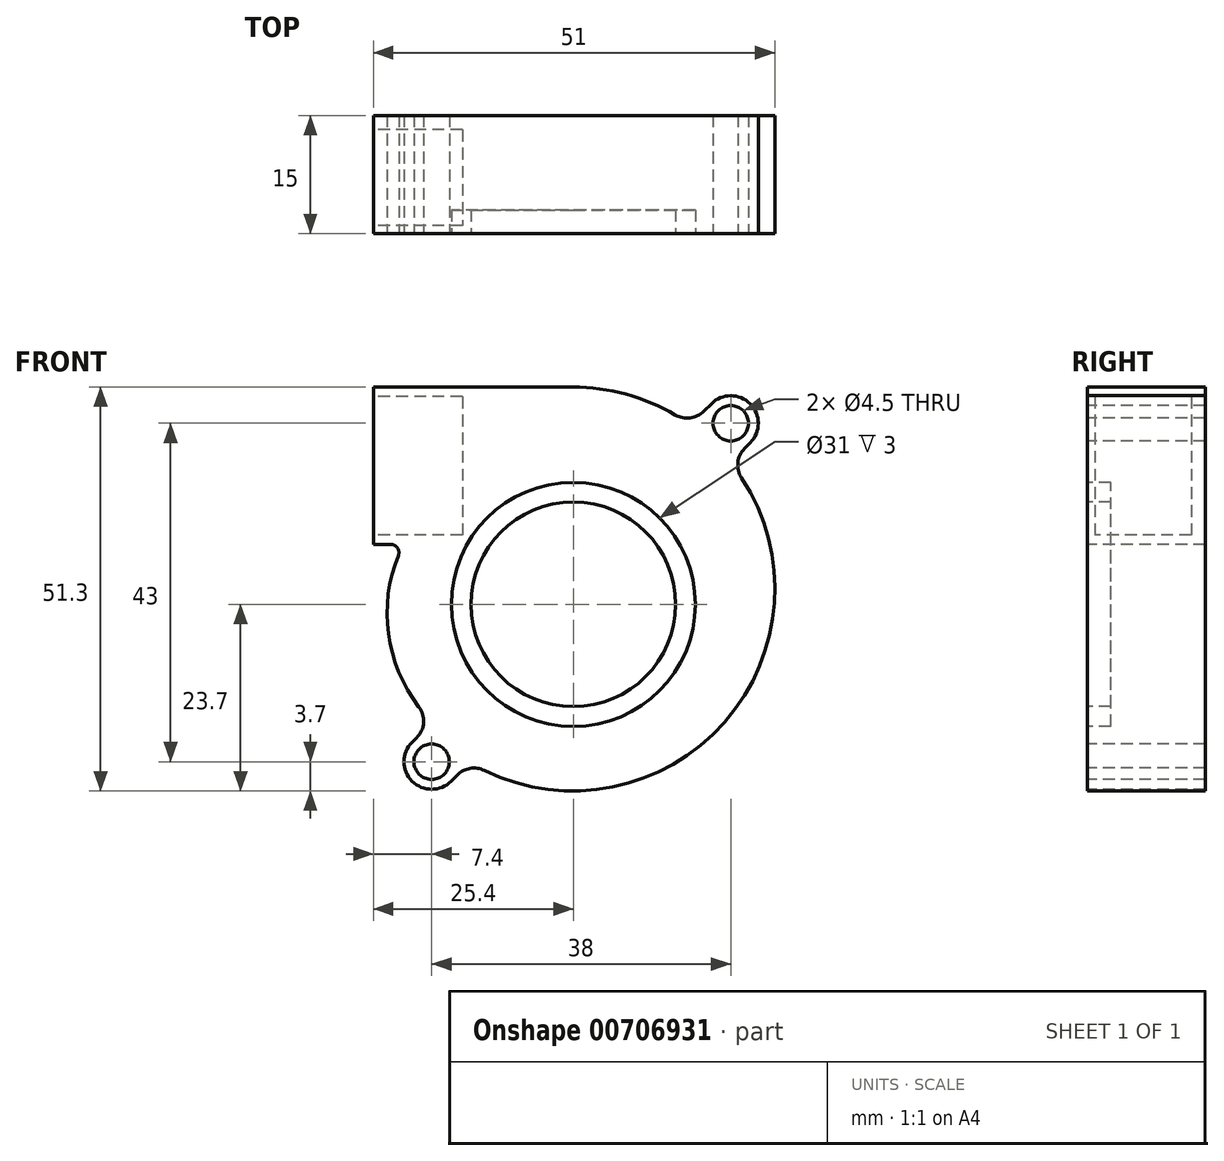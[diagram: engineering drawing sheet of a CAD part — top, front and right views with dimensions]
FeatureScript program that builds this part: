
annotation { "Feature Type Name" : "Feature", "Feature Type Description" : "" }
export const myFeature = defineFeature(function(context is Context, id is Id, definition is map)
    precondition{}
    {
        {
            var Q0;
            Q0=qCreatedBy(makeId("Front.planeOp"),FACE);
            var sketch = newSketch(context, id + "F0", { "sketchPlane" : qUnion([Q0])});
            skLineSegment(sketch, "E0", {"start": v(0, 39.18) * mm, "end": v(0, -45.98) * mm, "construction": true});
            skLineSegment(sketch, "E1", {"start": v(-59.51, 0) * mm, "end": v(60.38, 0) * mm, "construction": true});
            skCircle(sketch, "E2", {"center": v(0, 0) * mm, "radius": 13 * mm});
            skCircle(sketch, "E3", {"center": v(0, 0) * mm, "radius": 15.5 * mm});
            skCircle(sketch, "E4", {"center": v(20, 23) * mm, "radius": 2.25 * mm});
            skCircle(sketch, "E5", {"center": v(-18, -20) * mm, "radius": 2.25 * mm});
            skLineSegment(sketch, "E6.bottom", {"start": v(-25.4, 27.6) * mm, "end": v(0, 27.6) * mm});
            skLineSegment(sketch, "E6.top", {"start": v(-25.4, 7.6) * mm, "end": v(-21.61, 7.6) * mm});
            skLineSegment(sketch, "E6.left", {"start": v(-25.4, 27.6) * mm, "end": v(-25.4, 7.6) * mm});
            skLineSegment(sketch, "E7", {"start": v(-62.06, -23.7) * mm, "end": v(66.72, -23.7) * mm, "construction": true});
            skArc(sketch, "E8", {"start": v(-13.15, -20.1) * mm, "mid": v(19.31, -14.88) * mm, "end": v(19.95, 18) * mm});
            skArc(sketch, "E9", {"start": v(-20.47, -17.53) * mm, "mid": v(-20.47, -22.47) * mm, "end": v(-15.53, -22.47) * mm});
            skArc(sketch, "E10", {"start": v(22.47, 20.53) * mm, "mid": v(22.47, 25.47) * mm, "end": v(17.53, 25.47) * mm});
            skLineSegment(sketch, "E11", {"start": v(17.53, 25.47) * mm, "end": v(14.86, 22.81) * mm});
            skLineSegment(sketch, "E12", {"start": v(22.47, 20.53) * mm, "end": v(19.95, 18) * mm});
            skLineSegment(sketch, "E13", {"start": v(-20.47, -17.53) * mm, "end": v(-17.92, -14.97) * mm});
            skLineSegment(sketch, "E14", {"start": v(-15.53, -22.47) * mm, "end": v(-13.15, -20.1) * mm});
            skArc(sketch, "E15.trimOffspring", {"start": v(14.86, 22.81) * mm, "mid": v(7.78, 26.37) * mm, "end": v(-0.05, 27.6) * mm});
            skArc(sketch, "E16", {"start": v(-21.61, 7.6) * mm, "mid": v(-23.4, -4.28) * mm, "end": v(-17.92, -14.97) * mm});
            skSolve(sketch);
        }
        {
            var Q0;
            Q0=makeQuery(id+"F0.imprint","IMPRINT",FACE,{"disambiguationData":[TD([[makeQuery(id+"F0.imprint","IMPRINT",EDGE,{"derivedFrom":sQuery(id+"F0.wireOp",EDGE,"E3")}),-1.0]])]});
            var Q1;
            Q1=makeQuery(id+"F0.imprint","IMPRINT",FACE,{"disambiguationData":[TD([[makeQuery(id+"F0.imprint","IMPRINT",EDGE,{"derivedFrom":sQuery(id+"F0.wireOp",EDGE,"E2")}),1.0]])]});
            var Q2;
            Q2=makeQuery(id+"F0.imprint","IMPRINT",FACE,{"disambiguationData":[TD([[makeQuery(id+"F0.imprint","IMPRINT",EDGE,{"derivedFrom":sQuery(id+"F0.wireOp",EDGE,"E2")}),-1.0]])]});
            extrude(context, id + "F1", {"entities" : qUnion([Q0, Q1, Q2]), "oppositeDirection" : true, "depth" : 15 * mm});
        }
        {
            var Q0;
            Q0=makeQuery(id+"F0.imprint","IMPRINT",FACE,{"disambiguationData":[TD([[makeQuery(id+"F0.imprint","IMPRINT",EDGE,{"derivedFrom":sQuery(id+"F0.wireOp",EDGE,"E2")}),-1.0]])]});
            extrude(context, id + "F2", {"entities" : qUnion([Q0]), "operationType" : NewBodyOperationType.REMOVE, "oppositeDirection" : true, "depth" : 3 * mm});
        }
        {
            var Q0;
            Q0=makeQuery(id+"F1.opExtrude","SWEPT_FACE",FACE,{"disambiguationData":[OSD([sQuery(id+"F0.wireOp",EDGE,"E6.left")])]});
            var sketch = newSketch(context, id + "F3", { "sketchPlane" : qUnion([Q0])});
            skLineSegment(sketch, "E17.bottom", {"start": v(-13.2, 26.4) * mm, "end": v(-1, 26.4) * mm});
            skLineSegment(sketch, "E17.top", {"start": v(-13.2, 8.8) * mm, "end": v(-1, 8.8) * mm});
            skLineSegment(sketch, "E17.left", {"start": v(-13.2, 26.4) * mm, "end": v(-13.2, 8.8) * mm});
            skLineSegment(sketch, "E17.right", {"start": v(-1, 26.4) * mm, "end": v(-1, 8.8) * mm});
            skLineSegment(sketch, "E18", {"start": v(13.3, 0) * mm, "end": v(-29.9, 0) * mm, "construction": true});
            skSolve(sketch);
        }
        {
            var Q0;
            Q0=qSketchRegion(id+"F3",true);
            extrude(context, id + "F4", {"entities" : qUnion([Q0]), "operationType" : NewBodyOperationType.REMOVE, "oppositeDirection" : true, "depth" : 11.3 * mm});
        }
        {
            var Q0;
            Q0=makeQuery(id+"F1.opExtrude","SWEPT_EDGE",EDGE,{"disambiguationData":[OSD([sQuery(id+"F0.wireOp",EDGE,"E6.top"),sQuery(id+"F0.wireOp",EDGE,"E16")])]});
            fillet(context, id + "F5", {"entities" : qUnion([Q0]), "radius" : 1 * mm, "tangentPropagation" : true, "allowEdgeOverflow" : false});
        }
        {
            var Q0;
            Q0=makeQuery(id+"F1.opExtrude","SWEPT_EDGE",EDGE,{"disambiguationData":[OSD([sQuery(id+"F0.wireOp",EDGE,"E13"),sQuery(id+"F0.wireOp",EDGE,"E16")])]});
            var Q1;
            Q1=makeQuery(id+"F1.opExtrude","SWEPT_EDGE",EDGE,{"disambiguationData":[OSD([sQuery(id+"F0.wireOp",EDGE,"E8"),sQuery(id+"F0.wireOp",EDGE,"E14")])]});
            var Q2;
            Q2=makeQuery(id+"F1.opExtrude","SWEPT_EDGE",EDGE,{"disambiguationData":[OSD([sQuery(id+"F0.wireOp",EDGE,"E8"),sQuery(id+"F0.wireOp",EDGE,"E12")])]});
            var Q3;
            Q3=makeQuery(id+"F1.opExtrude","SWEPT_EDGE",EDGE,{"disambiguationData":[OSD([sQuery(id+"F0.wireOp",EDGE,"E11"),sQuery(id+"F0.wireOp",EDGE,"E15.trimOffspring")])]});
            fillet(context, id + "F6", {"entities" : qUnion([Q0, Q1, Q2, Q3]), "radius" : 3 * mm, "tangentPropagation" : true, "allowEdgeOverflow" : false});
        }
    });
